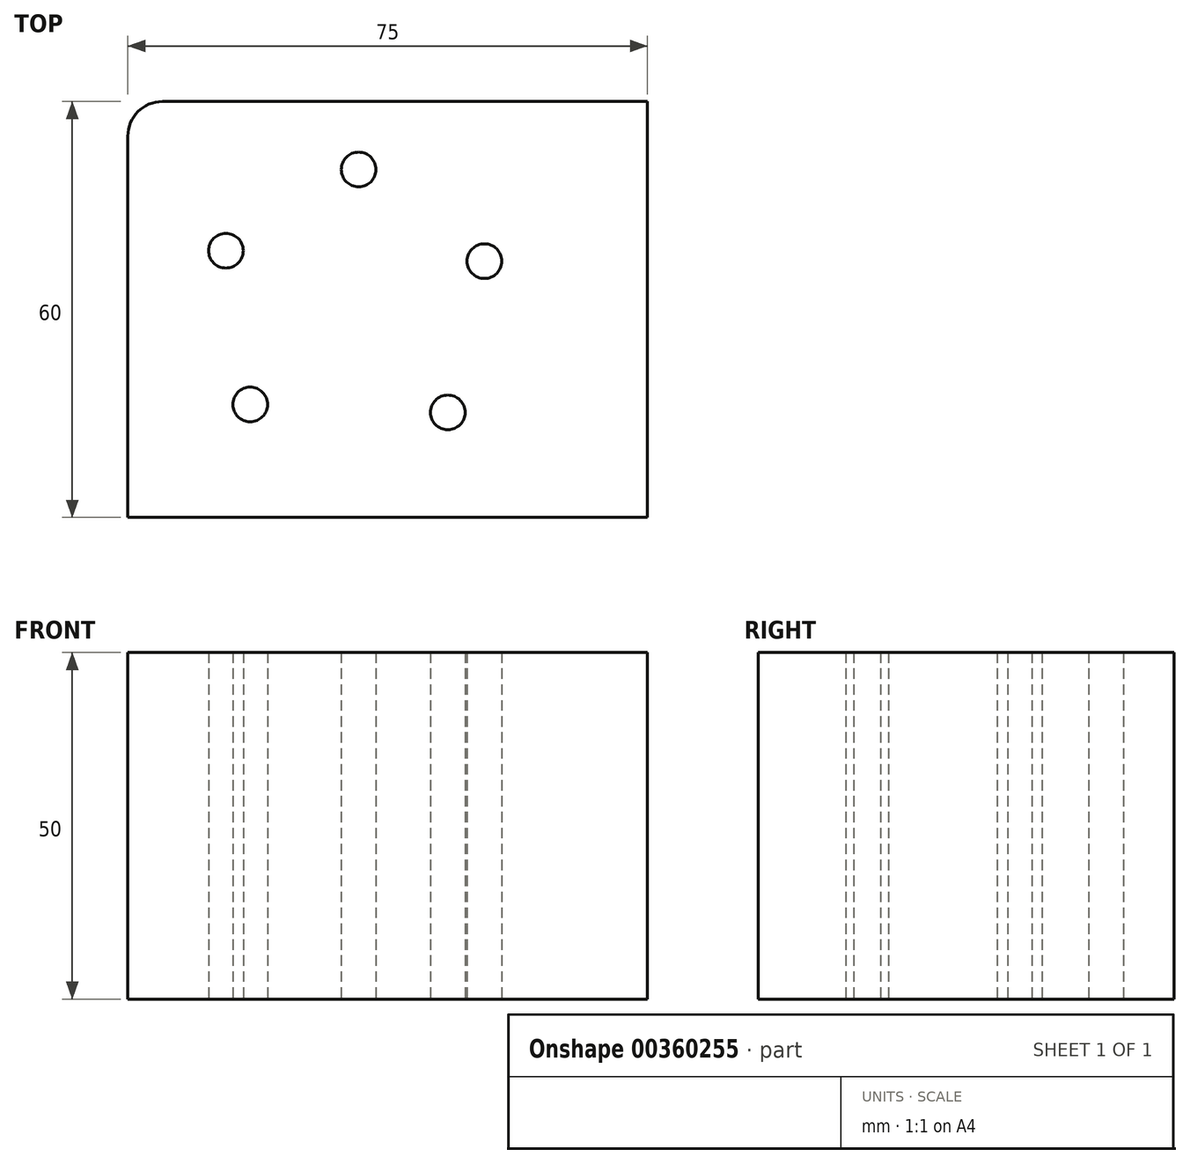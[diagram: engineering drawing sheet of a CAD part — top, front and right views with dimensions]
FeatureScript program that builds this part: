
annotation { "Feature Type Name" : "Feature", "Feature Type Description" : "" }
export const myFeature = defineFeature(function(context is Context, id is Id, definition is map)
    precondition{}
    {
        {
            var Q0;
            Q0=qCreatedBy(makeId("Top.planeOp"),FACE);
            var sketch = newSketch(context, id + "F0", { "sketchPlane" : qUnion([Q0])});
            skLineSegment(sketch, "E0.bottom", {"start": v(0, 0) * mm, "end": v(-75, 0) * mm});
            skLineSegment(sketch, "E0.top", {"start": v(0, 60) * mm, "end": v(-75, 60) * mm});
            skLineSegment(sketch, "E0.left", {"start": v(0, 0) * mm, "end": v(0, 60) * mm});
            skLineSegment(sketch, "E0.right", {"start": v(-75, 0) * mm, "end": v(-75, 60) * mm});
            skCircle(sketch, "E1", {"center": v(-57.34, 16.29) * mm, "radius": 2.5 * mm});
            skCircle(sketch, "E2.1.0", {"center": v(-60.84, 38.47) * mm, "radius": 2.5 * mm});
            skCircle(sketch, "E2.2.0", {"center": v(-41.69, 50.19) * mm, "radius": 2.5 * mm});
            skCircle(sketch, "E2.3.0", {"center": v(-23.53, 36.96) * mm, "radius": 2.5 * mm});
            skCircle(sketch, "E2.4.0", {"center": v(-28.82, 15.14) * mm, "radius": 2.5 * mm});
            skPoint(sketch, "E2.center", {"position": v(-42.5, 30) * mm});
            skLineSegment(sketch, "E2.anchor1", {"start": v(-42.5, 30) * mm, "end": v(-57.34, 16.29) * mm, "construction": true});
            skLineSegment(sketch, "E2.anchor2", {"start": v(-42.5, 30) * mm, "end": v(-28.82, 15.14) * mm, "construction": true});
            skSolve(sketch);
        }
        {
            var Q0;
            Q0 = qSketchRegion(id + "F0", true);
            extrude(context, id + "F1", {"entities" : qUnion([Q0]), "depth" : 50 * mm});
        }
        {
            var Q0;
            Q0=makeQuery(id+"F1.opExtrude","SWEPT_EDGE",EDGE,{"disambiguationData":[OSD([sQuery(id+"F0.wireOp",EDGE,"E0.top"),sQuery(id+"F0.wireOp",EDGE,"E0.right")])]});
            fillet(context, id + "F2", {"entities" : qUnion([Q0]), "radius" : 5 * mm, "tangentPropagation" : true, "allowEdgeOverflow" : false});
        }
    });
